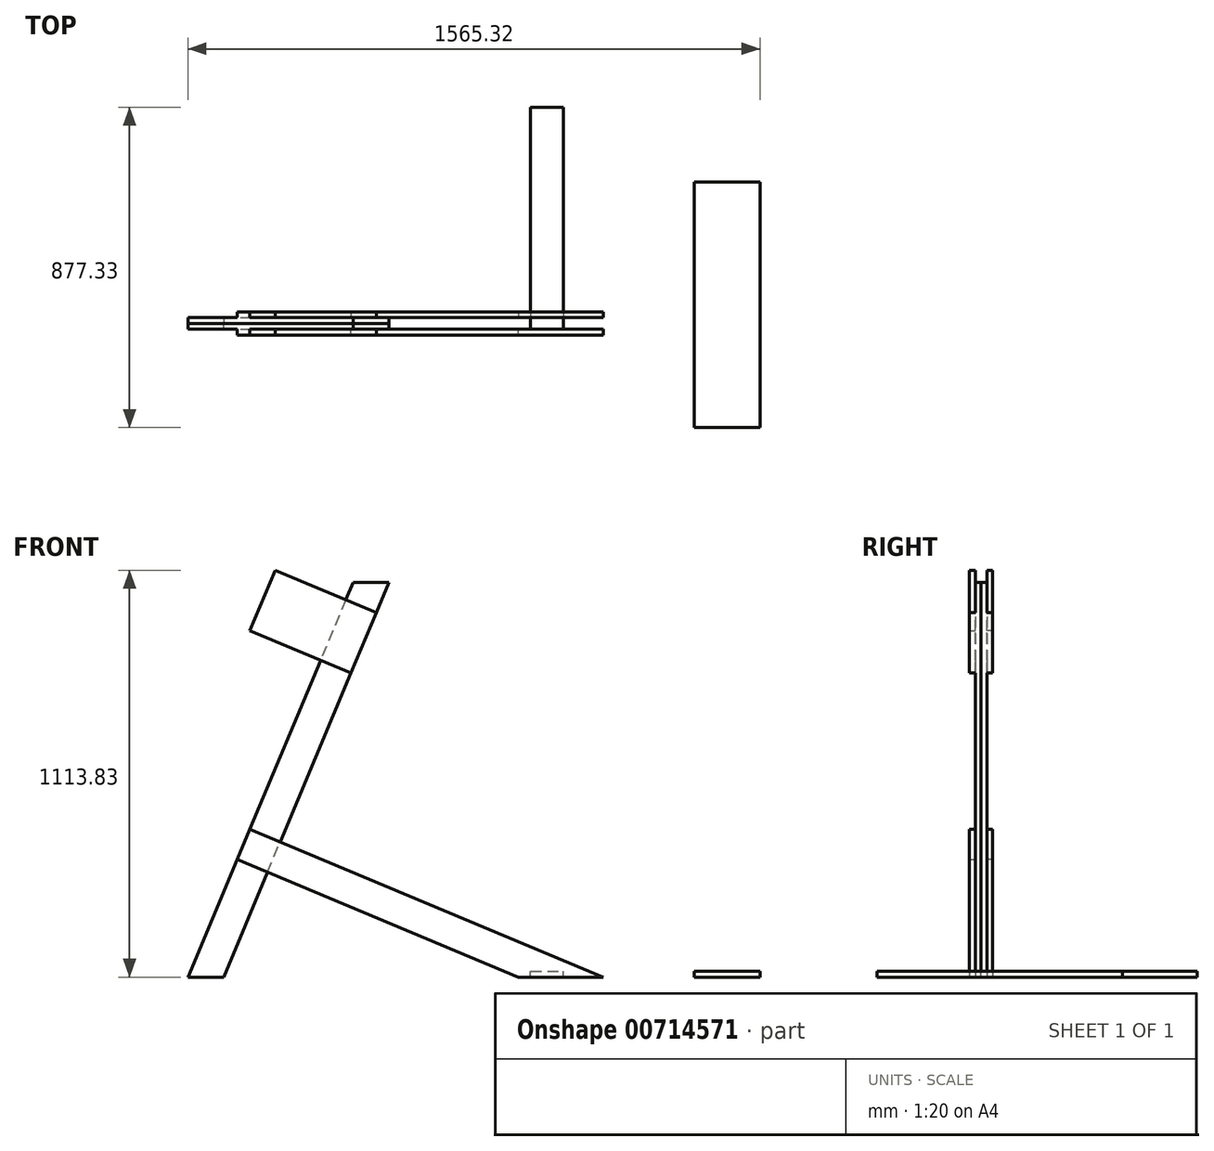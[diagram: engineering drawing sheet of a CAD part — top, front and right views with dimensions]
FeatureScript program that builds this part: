
annotation { "Feature Type Name" : "Feature", "Feature Type Description" : "" }
export const myFeature = defineFeature(function(context is Context, id is Id, definition is map)
    precondition{}
    {
        {
            var Q0;
            Q0=qCreatedBy(makeId("Front.planeOp"),FACE);
            var sketch = newSketch(context, id + "F0", { "sketchPlane" : qUnion([Q0])});
            skLineSegment(sketch, "E0", {"start": v(-1650.69, 0) * mm, "end": v(-1553.13, 0) * mm});
            skLineSegment(sketch, "E1", {"start": v(-1553.13, 0) * mm, "end": v(-1101.35, 1080) * mm});
            skLineSegment(sketch, "E2", {"start": v(-1101.35, 1080) * mm, "end": v(-1198.91, 1080) * mm});
            skLineSegment(sketch, "E3", {"start": v(-1198.91, 1080) * mm, "end": v(-1650.69, 0) * mm});
            skLineSegment(sketch, "E4", {"start": v(-1242.87, 741.7) * mm, "end": v(-1325.9, 776.43) * mm, "construction": true});
            skLineSegment(sketch, "E5", {"start": v(-1150.13, 1080) * mm, "end": v(-1150.13, 0) * mm, "construction": true});
            skSolve(sketch);
        }
        {
            var Q0;
            Q0 = qSketchRegion(id + "F0", true);
            extrude(context, id + "F1", {"entities" : qUnion([Q0]), "depth" : 16 * mm, "offsetDistance" : 25 * mm});
        }
        {
            var Q0;
            Q0=makeQuery(id+"F1.opExtrude","CAP_FACE",FACE,{"disambiguationData":[OSD([sQuery(id+"F0.wireOp",EDGE,"E0"),sQuery(id+"F0.wireOp",EDGE,"E1"),sQuery(id+"F0.wireOp",EDGE,"E2"),sQuery(id+"F0.wireOp",EDGE,"E3")])],"isStart":false});
            var sketch = newSketch(context, id + "F2", { "sketchPlane" : qUnion([Q0])});
            skLineSegment(sketch, "E6", {"start": v(-1553.13, 0) * mm, "end": v(-381.06, 0) * mm, "construction": true});
            skLineSegment(sketch, "E7", {"start": v(-1150.13, 1080) * mm, "end": v(-1150.13, 0) * mm, "construction": true});
            skPoint(sketch, "E8", {"position": v(-747.14, 0) * mm});
            skLineSegment(sketch, "E9", {"start": v(-747.14, 0) * mm, "end": v(-1516.13, 321.67) * mm});
            skLineSegment(sketch, "E10", {"start": v(-1516.13, 321.67) * mm, "end": v(-1481.4, 404.7) * mm});
            skLineSegment(sketch, "E11", {"start": v(-1481.4, 404.7) * mm, "end": v(-513.92, 0) * mm});
            skLineSegment(sketch, "E12", {"start": v(-513.92, 0) * mm, "end": v(-747.14, 0) * mm});
            skSolve(sketch);
        }
        {
            var Q0;
            Q0 = qSketchRegion(id + "F2", true);
            extrude(context, id + "F3", {"entities" : qUnion([Q0]), "operationType" : NewBodyOperationType.ADD, "depth" : 16 * mm, "offsetDistance" : 25 * mm});
        }
        {
            var Q0;
            {var subQ2=sQuery(id+"F0.wireOp",EDGE,"E3");var subQ3=sQuery(id+"F0.wireOp",EDGE,"E2");var subQ4=sQuery(id+"F0.wireOp",EDGE,"E1");Q0=makeQuery(id+"F3.boolean.opBoolean","SPLIT",FACE,{"disambiguationData":[TD([makeQuery(id+"F1.opExtrude","SWEPT_FACE",FACE,{"disambiguationData":[OSD([subQ3])]})])],"derivedFrom":makeQuery(id+"F1.opExtrude","CAP_FACE",FACE,{"disambiguationData":[OSD([sQuery(id+"F0.wireOp",EDGE,"E0"),subQ4,subQ3,subQ2])],"isStart":false})});}
            var sketch = newSketch(context, id + "F4", { "sketchPlane" : qUnion([Q0])});
            skSolve(sketch);
        }
        {
            var Q0;
            {var subQ0=sQuery(id+"F0.wireOp",EDGE,"E2");Q0=makeQuery(id+"F4.imprint","IMPRINT",FACE,{"disambiguationData":[TD([[makeQuery(id+"F4.imprint","IMPRINT",EDGE,{"derivedFrom":makeQuery(id+"F1.opExtrude","CAP_EDGE",EDGE,{"disambiguationData":[OSD([subQ0])],"isStart":false})}),1.0]])]});}
            var sketch = newSketch(context, id + "F5", { "sketchPlane" : qUnion([Q0])});
            skLineSegment(sketch, "E13", {"start": v(-1150.13, 1080) * mm, "end": v(-1246.6, 849.37) * mm, "construction": true});
            skLineSegment(sketch, "E14", {"start": v(-1246.6, 849.37) * mm, "end": v(-1205.1, 832) * mm, "construction": true});
            skLineSegment(sketch, "E15", {"start": v(-1205.1, 832) * mm, "end": v(-1481.86, 947.77) * mm});
            skLineSegment(sketch, "E16", {"start": v(-1481.86, 947.77) * mm, "end": v(-1412.4, 1113.83) * mm});
            skLineSegment(sketch, "E17", {"start": v(-1412.4, 1113.83) * mm, "end": v(-1135.63, 998.06) * mm});
            skLineSegment(sketch, "E18", {"start": v(-1135.63, 998.06) * mm, "end": v(-1205.1, 832) * mm});
            skSolve(sketch);
        }
        {
            var Q0;
            Q0 = qSketchRegion(id + "F5", true);
            extrude(context, id + "F6", {"entities" : qUnion([Q0]), "operationType" : NewBodyOperationType.ADD, "depth" : 16 * mm, "offsetDistance" : 25 * mm});
        }
        {
            var Q0;
            Q0=makeQuery(id+"F1.opExtrude","SWEPT_BODY",BODY,{"disambiguationData":[OSD([sQuery(id+"F0.wireOp",EDGE,"E0"),sQuery(id+"F0.wireOp",EDGE,"E1"),sQuery(id+"F0.wireOp",EDGE,"E2"),sQuery(id+"F0.wireOp",EDGE,"E3")])]});
            transform(context, id + "F7", {"entities" : qUnion([Q0]), "transformType" : TransformType.TRANSLATION_3D, "dx" : 0 * mm, "dy" : 0 * mm, "dz" : 0 * mm, "makeCopy" : true});
        }
        {
            var Q0;
            Q0=makeQuery(id+"F7.opPattern","COPY",BODY,{"derivedFrom":makeQuery(id+"F1.opExtrude","SWEPT_BODY",BODY,{"disambiguationData":[OSD([sQuery(id+"F0.wireOp",EDGE,"E0"),sQuery(id+"F0.wireOp",EDGE,"E1"),sQuery(id+"F0.wireOp",EDGE,"E2"),sQuery(id+"F0.wireOp",EDGE,"E3")])]}),"instanceName":"1"});
            var Q1;
            Q1=qCreatedBy(makeId("Front.planeOp"),FACE);
            mirror(context, id + "F8", {"entities" : qUnion([Q0]), "mirrorPlane" : qUnion([Q1])});
        }
        {
            var Q0;
            Q0=makeQuery(id+"F7.opPattern","COPY",BODY,{"derivedFrom":makeQuery(id+"F1.opExtrude","SWEPT_BODY",BODY,{"disambiguationData":[OSD([sQuery(id+"F0.wireOp",EDGE,"E0"),sQuery(id+"F0.wireOp",EDGE,"E1"),sQuery(id+"F0.wireOp",EDGE,"E2"),sQuery(id+"F0.wireOp",EDGE,"E3")])]}),"instanceName":"1"});
            deleteBodies(context, id + "F9", {"entities" : qUnion([Q0])});
        }
        {
            var Q0;
            Q0=makeQuery(id+"F3.opExtrude","CAP_FACE",FACE,{"disambiguationData":[OSD([sQuery(id+"F2.wireOp",EDGE,"E9"),sQuery(id+"F2.wireOp",EDGE,"E10"),sQuery(id+"F2.wireOp",EDGE,"E11"),sQuery(id+"F2.wireOp",EDGE,"E12")])],"isStart":true});
            var sketch = newSketch(context, id + "F10", { "sketchPlane" : qUnion([Q0])});
            skLineSegment(sketch, "E19.bottom", {"start": v(712.98, 0) * mm, "end": v(622.98, 0) * mm});
            skLineSegment(sketch, "E19.top", {"start": v(712.98, 16) * mm, "end": v(622.98, 16) * mm});
            skLineSegment(sketch, "E19.left", {"start": v(712.98, 0) * mm, "end": v(712.98, 16) * mm});
            skLineSegment(sketch, "E19.right", {"start": v(622.98, 0) * mm, "end": v(622.98, 16) * mm});
            skSolve(sketch);
        }
        {
            var Q0;
            Q0 = qSketchRegion(id + "F10", true);
            extrude(context, id + "F11", {"entities" : qUnion([Q0]), "depth" : (640 - 32) * mm, "offsetDistance" : 25 * mm});
        }
        {
            var Q0;
            Q0=qCreatedBy(makeId("Top.planeOp"),FACE);
            var sketch = newSketch(context, id + "F12", { "sketchPlane" : qUnion([Q0])});
            skLineSegment(sketch, "E20.bottom", {"start": v(-85.37, -285.33) * mm, "end": v(-265.37, -285.33) * mm});
            skLineSegment(sketch, "E20.top", {"start": v(-85.37, 386.67) * mm, "end": v(-265.37, 386.67) * mm});
            skLineSegment(sketch, "E20.left", {"start": v(-85.37, -285.33) * mm, "end": v(-85.37, 386.67) * mm});
            skLineSegment(sketch, "E20.right", {"start": v(-265.37, -285.33) * mm, "end": v(-265.37, 386.67) * mm});
            skSolve(sketch);
        }
        {
            var Q0;
            Q0 = qSketchRegion(id + "F12", true);
            extrude(context, id + "F13", {"entities" : qUnion([Q0]), "depth" : 16 * mm, "offsetDistance" : 25 * mm});
        }
    });
